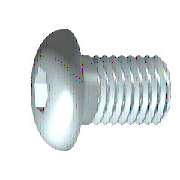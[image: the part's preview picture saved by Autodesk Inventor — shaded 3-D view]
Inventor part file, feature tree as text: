
AUTODESK INVENTOR PART (.ipt)
format: ipt  version: 2025 (Build 290162010, 162A)  size: 199,680 bytes
history: native  units: mm (DEFAULTED — no unit token found)
features: extrude x1, plane x1, fillet x1
ambient origin geometry x7: Origin, YZ Plane, XY Plane, X Axis, Y Axis, Z Axis, Center Point
bodies: Solid1 (feature_tree), Body (feature_tree)
feature tree (3):
  extrude  "Slot"  Depth=8.5mm
  plane  "Work Plane1"
  fillet  "Fillet2"  Radius=0.306825mm
